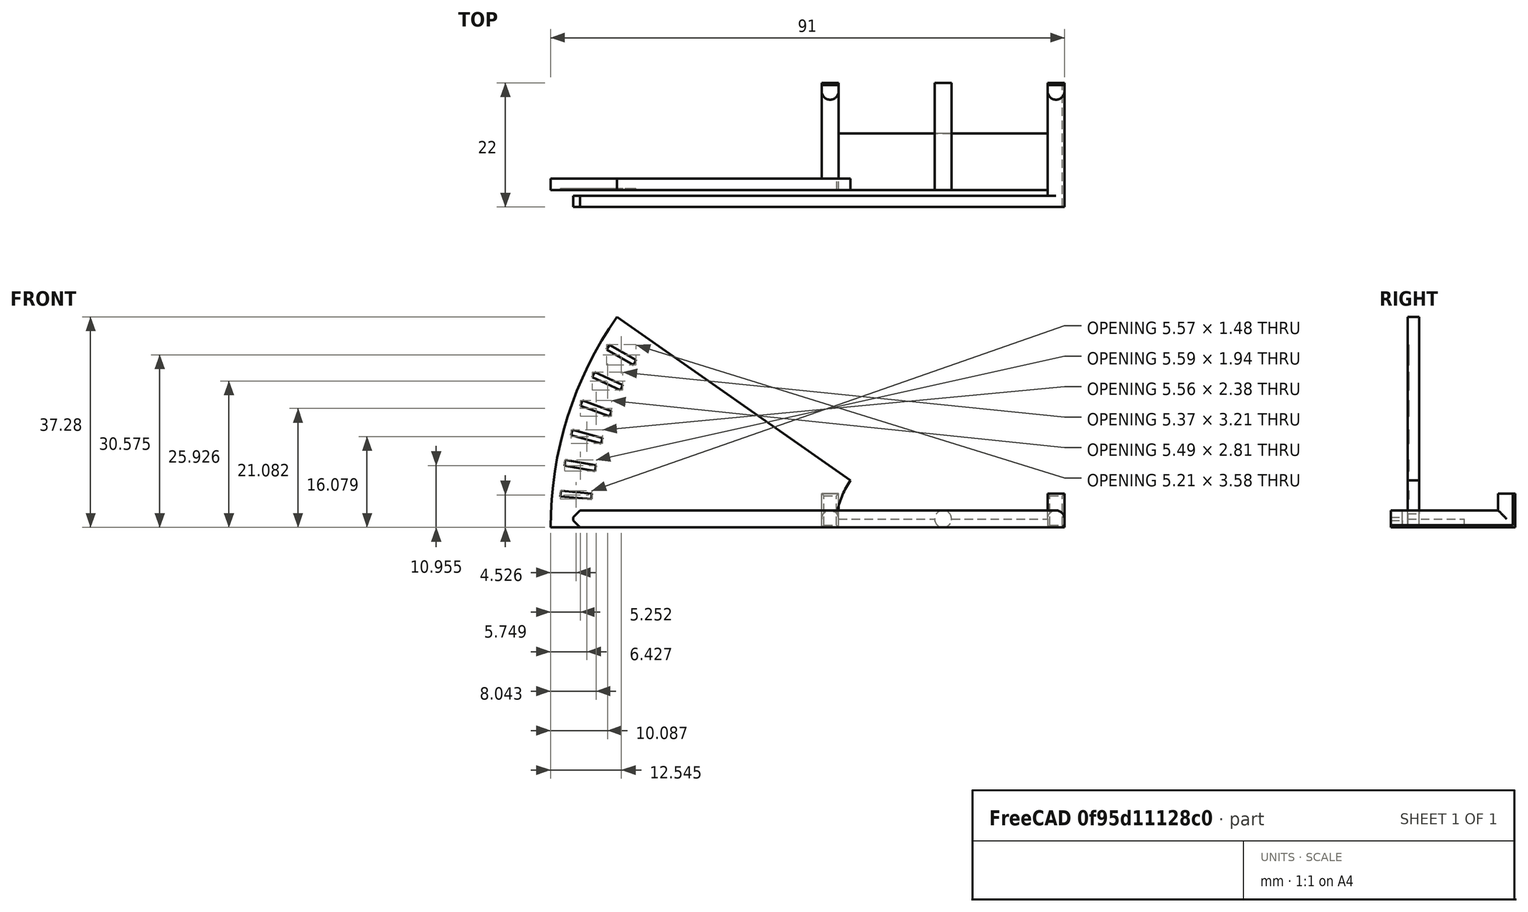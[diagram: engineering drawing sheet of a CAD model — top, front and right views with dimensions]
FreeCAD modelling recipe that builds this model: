
FCSTD DOCUMENT  (FreeCAD 0.18R16146 (Git))
Label: belt-tension-meter
License: All rights reserved
LicenseURL: http://en.wikipedia.org/wiki/All_rights_reserved
objects: Part::Box×12, Part::Cylinder×8, Part::Cut×3, Part::MultiFuse×2, Part::Chamfer×2, Mesh::Feature×1, Part::Fillet×1, Part::Feature×1
note: 29 computed .brp shape members not serialized (recipe doc carries the construction recipe); baked Part::Feature solids carry a one-line shape summary decoded from their .brp

FEATURE [Mesh::Feature] belt
  Placement = pos=(-127.5,-93.9,0) rot=(0,0,1;0rad)
FEATURE [Part::Cylinder] Cylinder
  Angle = 35
  AttacherType = Attacher::AttachEngine3D
  Height = 2
  Placement = pos=(17,3,-1e-15) rot=(0,0.707107,0.707107;3.14159rad)
  Radius = 65
FEATURE [Part::Cylinder] Cylinder001
  Angle = 360
  AttacherType = Attacher::AttachEngine3D
  Height = 2
  Placement = pos=(17,3,-1e-15) rot=(-1,0,0;1.5708rad)
  Radius = 14.5
FEATURE [Part::Cut] Cut
  Base = -> Cylinder
  Tool = -> Cylinder001
FEATURE [Part::Box] Box  label="Cube"
  AttacherType = Attacher::AttachEngine3D
  Height = 3
  Length = 87
  Placement = pos=(-44,0,0) rot=(0,0,1;0rad)
  Width = 2
FEATURE [Part::Cylinder] Cylinder002
  Angle = 360
  AttacherType = Attacher::AttachEngine3D
  Height = 19
  Placement = pos=(1.5,3,1.5) rot=(-1,0,0;1.5708rad)
  Radius = 1.5
FEATURE [Part::Cylinder] Cylinder003
  Angle = 360
  AttacherType = Attacher::AttachEngine3D
  Height = 4.5
  Placement = pos=(1.5,20.5,1.5) rot=(0,0,1;0rad)
  Radius = 1.5
FEATURE [Part::Cylinder] Cylinder004
  Angle = 360
  AttacherType = Attacher::AttachEngine3D
  Height = 19
  Placement = pos=(21.5,3,1.5) rot=(-1,0,0;1.5708rad)
  Radius = 1.5
FEATURE [Part::Cylinder] Cylinder005
  Angle = 360
  AttacherType = Attacher::AttachEngine3D
  Height = 22
  Placement = pos=(41.5,0,1.5) rot=(-1,0,0;1.5708rad)
  Radius = 1.5
FEATURE [Part::Cylinder] Cylinder006
  Angle = 360
  AttacherType = Attacher::AttachEngine3D
  Height = 4.5
  Placement = pos=(41.5,20.5,1.5) rot=(0,0,1;0rad)
  Radius = 1.5
FEATURE [Part::Box] Box001  label="Cube001"
  AttacherType = Attacher::AttachEngine3D
  Height = 1.5
  Length = 43
  Placement = pos=(0,3,0) rot=(0,0,1;0rad)
  Width = 10
FEATURE [Part::Box] Box002  label="Cube002"
  AttacherType = Attacher::AttachEngine3D
  Height = 1.5
  Length = 3
  Placement = pos=(40,2,0) rot=(0,0,1;0rad)
  Width = 20
FEATURE [Part::Box] Box003  label="Cube003"
  AttacherType = Attacher::AttachEngine3D
  Height = 1.5
  Length = 3
  Placement = pos=(0,3,0) rot=(0,0,1;0rad)
  Width = 19
FEATURE [Part::Box] Box004  label="Cube004"
  AttacherType = Attacher::AttachEngine3D
  Height = 6
  Length = 3
  Placement = pos=(0,20.5,0) rot=(0,0,1;0rad)
  Width = 1.5
FEATURE [Part::Box] Box005  label="Cube005"
  AttacherType = Attacher::AttachEngine3D
  Height = 6
  Length = 3
  Placement = pos=(40,20.5,0) rot=(0,0,1;0rad)
  Width = 1.5
FEATURE [Part::Cylinder] Cylinder007
  Angle = 360
  AttacherType = Attacher::AttachEngine3D
  Height = 15
  Placement = pos=(17,3,-1e-15) rot=(-1,0,0;1.5708rad)
  Radius = 58
FEATURE [Part::Box] Box007  label="Cube007"
  AttacherType = Attacher::AttachEngine3D
  Height = 63
  Length = 1
  Placement = pos=(16.5,3,0) rot=(0,-1,0;1.48353rad)
  Width = 0.5
FEATURE [Part::Box] Box008  label="Cube008"
  AttacherType = Attacher::AttachEngine3D
  Height = 63
  Length = 1
  Placement = pos=(16.5,3,0) rot=(0,-1,0;1.39626rad)
  Width = 0.5
FEATURE [Part::Box] Box009  label="Cube009"
  AttacherType = Attacher::AttachEngine3D
  Height = 63
  Length = 1
  Placement = pos=(16.5,3,0) rot=(0,-1,0;1.309rad)
  Width = 0.5
FEATURE [Part::Box] Box010  label="Cube010"
  AttacherType = Attacher::AttachEngine3D
  Height = 63
  Length = 1
  Placement = pos=(16.5,3,0) rot=(0,-1,0;1.22173rad)
  Width = 0.5
FEATURE [Part::Box] Box011  label="Cube011"
  AttacherType = Attacher::AttachEngine3D
  Height = 63
  Length = 1
  Placement = pos=(16.5,3,0) rot=(0,-1,0;1.13446rad)
  Width = 0.5
FEATURE [Part::Box] Box012  label="Cube012"
  AttacherType = Attacher::AttachEngine3D
  Height = 63
  Length = 1
  Placement = pos=(16.5,3,0) rot=(0,-1,0;1.0472rad)
  Width = 0.5
FEATURE [Part::MultiFuse] Fusion
  Shapes = -> [Box012,Box011,Box010,Box009,Box008,Box007]
FEATURE [Part::Cut] Cut001
  Base = -> Fusion
  Placement = pos=(0,-0.25,0) rot=(0,0,1;0rad)
  Tool = -> Cylinder007
FEATURE [Part::Cut] Cut002
  Base = -> Cut
  Tool = -> Cut001
FEATURE [Part::Chamfer] Chamfer
  Base = -> Box
  Edges = 2 edges r=1.2: [Edge2,Edge4]
FEATURE [Part::Fillet] Fillet
  Base = -> Chamfer
  Edges = 1 edges r=1.5: [Edge18]
FEATURE [Part::MultiFuse] Fusion001
  Shapes = -> [Fillet,Cylinder002,Cylinder006,Box005,Cylinder005,Box004,Cylinder004,Box003,Cylinder003,Box001,Box002,Cut002]
FEATURE [Part::Feature] Fusion001001  label="Fusion002"
  shape: bbox 91 x 22 x 37.28 mm, 61 faces (baked)
FEATURE [Part::Chamfer] Chamfer001
  Base = -> Fusion001001
  Edges = 9 edges r=0.4: [Edge39,Edge41,Edge42,Edge43,Edge47,Edge48,Edge60,Edge62,Edge63]
